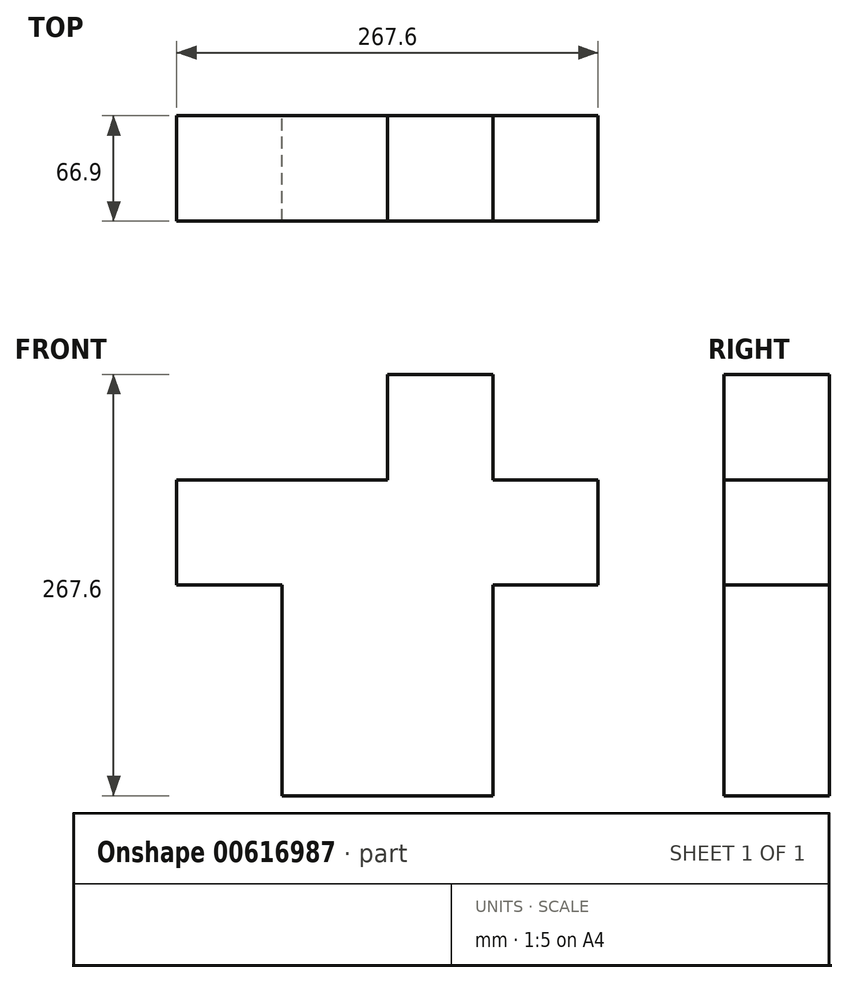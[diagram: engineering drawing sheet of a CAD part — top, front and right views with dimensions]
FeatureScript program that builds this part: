
annotation { "Feature Type Name" : "Feature", "Feature Type Description" : "" }
export const myFeature = defineFeature(function(context is Context, id is Id, definition is map)
    precondition{}
    {
        {
            var Q0;
            Q0=qCreatedBy(makeId("Front.planeOp"),FACE);
            var sketch = newSketch(context, id + "F0", { "sketchPlane" : qUnion([Q0])});
            skLineSegment(sketch, "E0", {"start": v(-200.7, 126.92) * mm, "end": v(-66.9, 126.92) * mm});
            skLineSegment(sketch, "E1", {"start": v(-66.9, 126.92) * mm, "end": v(-66.9, 193.82) * mm});
            skLineSegment(sketch, "E2", {"start": v(0, 193.82) * mm, "end": v(-66.9, 193.82) * mm});
            skLineSegment(sketch, "E3", {"start": v(0, 193.82) * mm, "end": v(0, 126.92) * mm});
            skLineSegment(sketch, "E4", {"start": v(0, 126.92) * mm, "end": v(66.9, 126.92) * mm});
            skLineSegment(sketch, "E5", {"start": v(66.9, 60.02) * mm, "end": v(66.9, 126.92) * mm});
            skLineSegment(sketch, "E6", {"start": v(66.9, 60.02) * mm, "end": v(0, 60.02) * mm});
            skLineSegment(sketch, "E7", {"start": v(0, -73.78) * mm, "end": v(0, 60.02) * mm});
            skLineSegment(sketch, "E8", {"start": v(0, -73.78) * mm, "end": v(-133.8, -73.78) * mm});
            skLineSegment(sketch, "E9", {"start": v(-133.8, -73.78) * mm, "end": v(-133.8, 60.02) * mm});
            skLineSegment(sketch, "E10", {"start": v(-200.7, 60.02) * mm, "end": v(-133.8, 60.02) * mm});
            skLineSegment(sketch, "E11", {"start": v(-200.7, 60.02) * mm, "end": v(-200.7, 126.92) * mm});
            skSolve(sketch);
        }
        {
            var Q0;
            Q0 = qSketchRegion(id + "F0", true);
            extrude(context, id + "F1", {"entities" : qUnion([Q0]), "depth" : 66.9 * mm, "offsetDistance" : 25 * mm});
        }
    });
